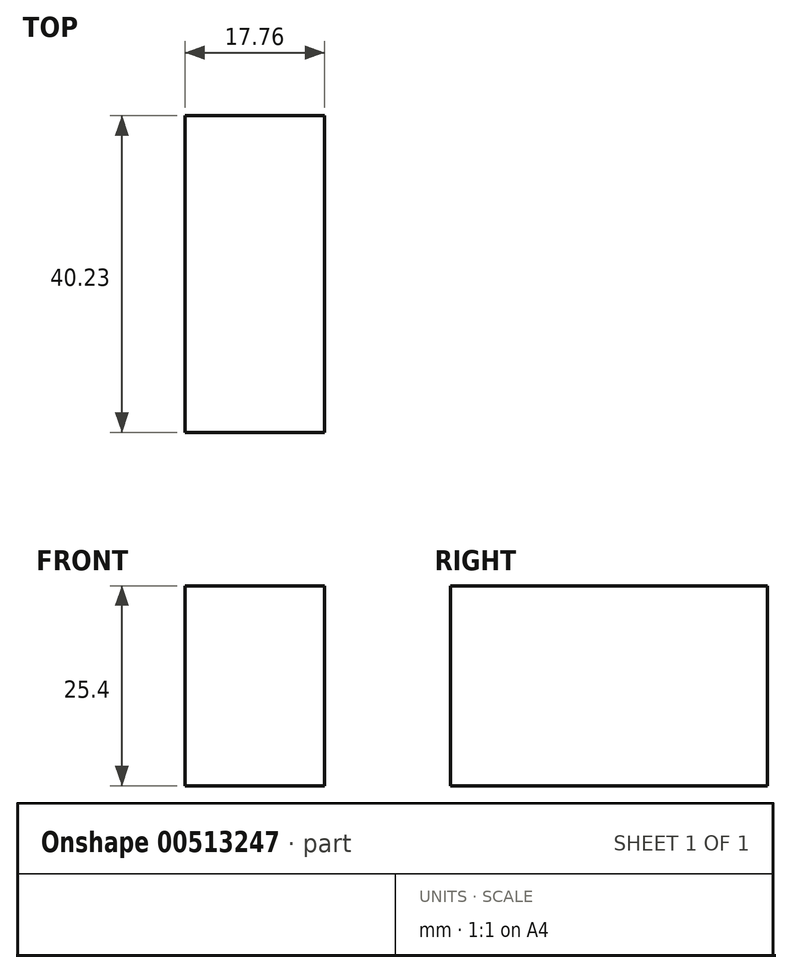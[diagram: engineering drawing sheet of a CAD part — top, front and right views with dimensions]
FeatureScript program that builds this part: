
annotation { "Feature Type Name" : "Feature", "Feature Type Description" : "" }
export const myFeature = defineFeature(function(context is Context, id is Id, definition is map)
    precondition{}
    {
        {
            var Q0;
            Q0=qCreatedBy(makeId("Top.planeOp"),FACE);
            var sketch = newSketch(context, id + "F0", { "sketchPlane" : qUnion([Q0])});
            skLineSegment(sketch, "E0.bottom", {"start": v(-12.98, -26.85) * mm, "end": v(-30.74, -26.85) * mm});
            skLineSegment(sketch, "E0.top", {"start": v(-12.98, 13.38) * mm, "end": v(-30.74, 13.38) * mm});
            skLineSegment(sketch, "E0.left", {"start": v(-12.98, -26.85) * mm, "end": v(-12.98, 13.38) * mm});
            skLineSegment(sketch, "E0.right", {"start": v(-30.74, -26.85) * mm, "end": v(-30.74, 13.38) * mm});
            skSolve(sketch);
        }
        {
            var Q0;
            Q0 = qSketchRegion(id + "F0", true);
            var Q1;
            Q1=makeQuery(id+"F0.imprint","IMPRINT",FACE,{"disambiguationData":[TD([[makeQuery(id+"F0.imprint","IMPRINT",EDGE,{"derivedFrom":sQuery(id+"F0.wireOp",EDGE,"E0.bottom")}),-1.0]])]});
            extrude(context, id + "F1", {"entities" : qUnion([Q0, Q1]), "depth" : 25.4 * mm});
        }
    });
